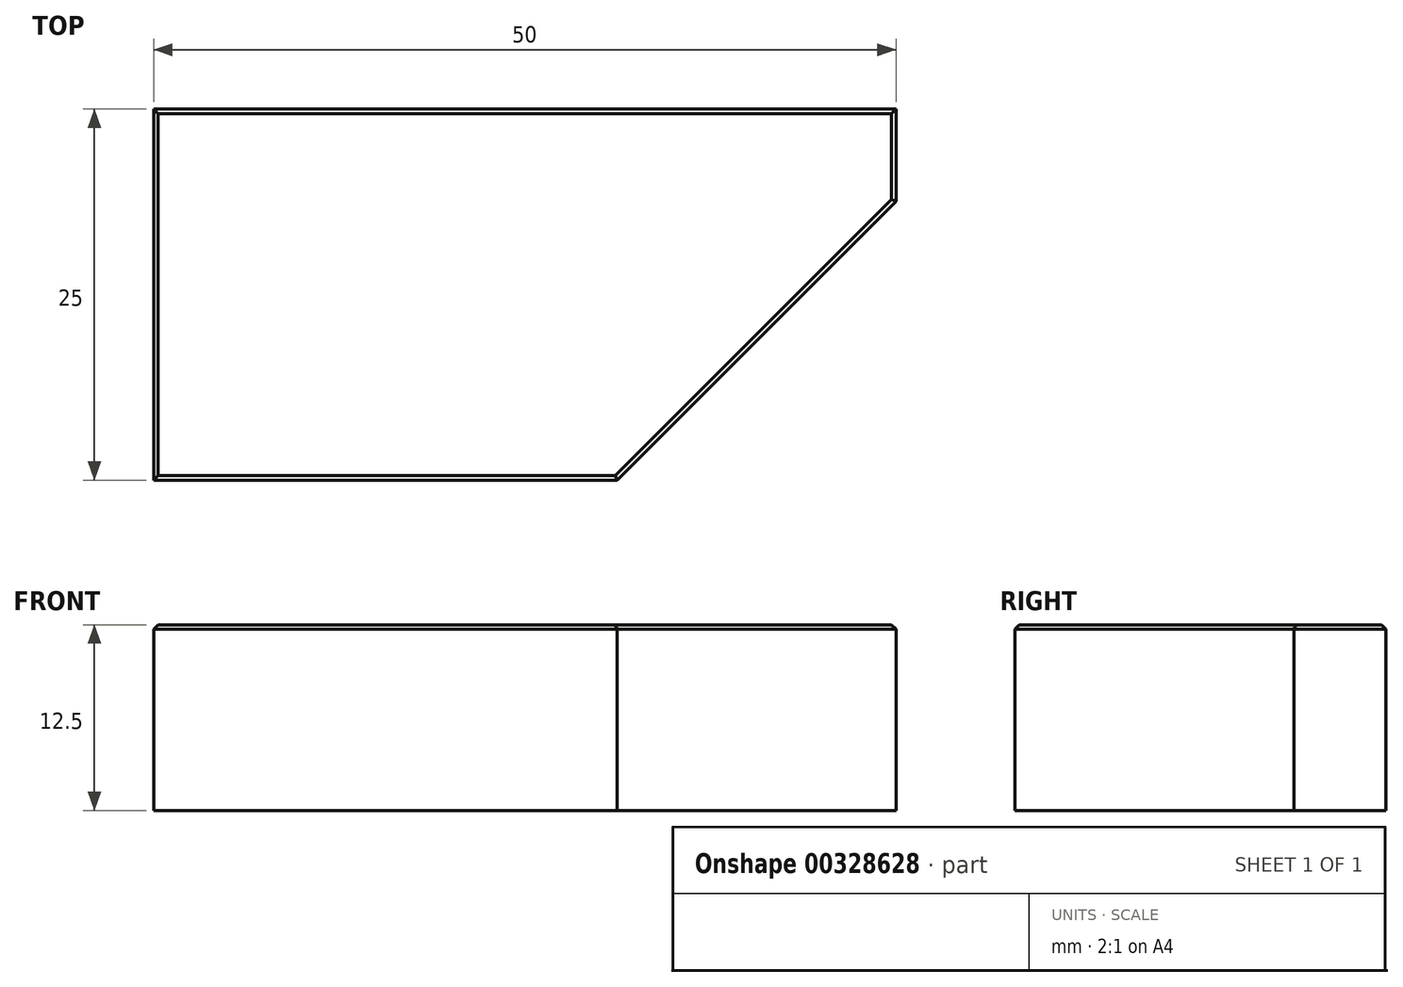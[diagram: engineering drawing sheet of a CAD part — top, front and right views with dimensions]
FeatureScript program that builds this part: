
annotation { "Feature Type Name" : "Feature", "Feature Type Description" : "" }
export const myFeature = defineFeature(function(context is Context, id is Id, definition is map)
    precondition{}
    {
        {
            var Q0;
            Q0=qCreatedBy(makeId("Top.planeOp"),FACE);
            var sketch = newSketch(context, id + "F0", { "sketchPlane" : qUnion([Q0])});
            skLineSegment(sketch, "E0.bottom", {"start": v(25, 12.5) * mm, "end": v(-25, 12.5) * mm});
            skLineSegment(sketch, "E0.top", {"start": v(6.2, -12.5) * mm, "end": v(-25, -12.5) * mm});
            skLineSegment(sketch, "E0.left", {"start": v(25, 12.5) * mm, "end": v(25, 6.3) * mm});
            skLineSegment(sketch, "E0.right", {"start": v(-25, 12.5) * mm, "end": v(-25, -12.5) * mm});
            skPoint(sketch, "E0.middle", {"position": v(0, 0) * mm});
            skLineSegment(sketch, "E1", {"start": v(6.2, -12.5) * mm, "end": v(25, 6.3) * mm});
            skSolve(sketch);
        }
        {
            var Q0;
            Q0=qSketchRegion(id+"F0",true);
            extrude(context, id + "F1", {"entities" : qUnion([Q0]), "oppositeDirection" : true, "depth" : 12.5 * mm});
        }
        {
            var Q0;
            Q0=makeQuery(id+"F1.opExtrude","CAP_FACE",FACE,{"disambiguationData":[OSD([sQuery(id+"F0.wireOp",EDGE,"E0.bottom"),sQuery(id+"F0.wireOp",EDGE,"E0.top"),sQuery(id+"F0.wireOp",EDGE,"E0.left"),sQuery(id+"F0.wireOp",EDGE,"E0.right")])],"isStart":true});
            chamfer(context, id + "F2", {"entities" : qUnion([Q0]), "width" : .3 * mm, "tangentPropagation" : true});
        }
    });
